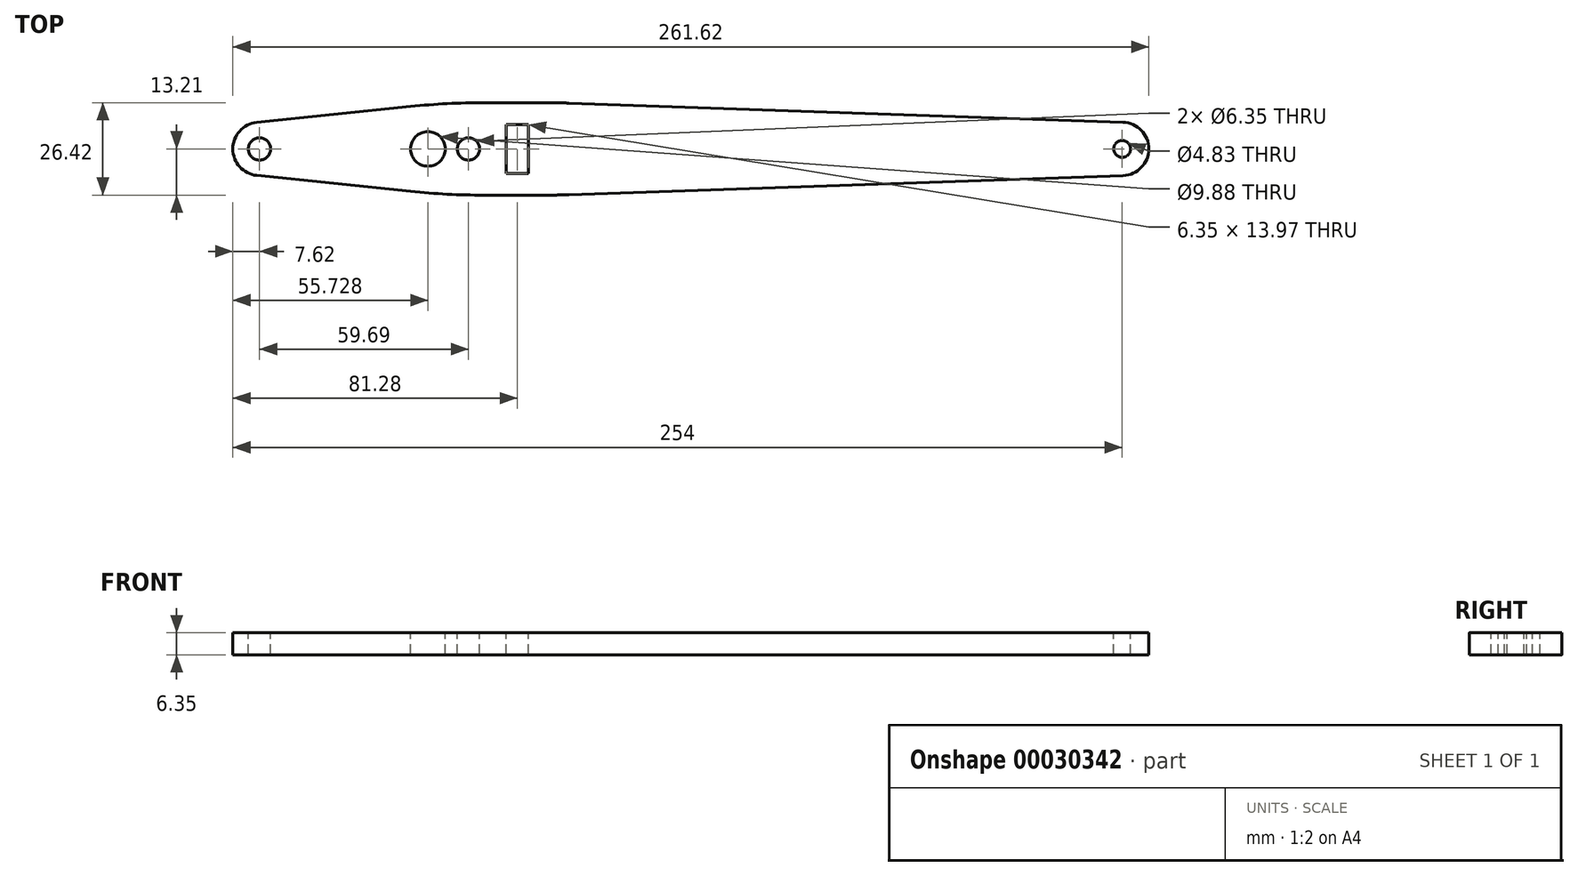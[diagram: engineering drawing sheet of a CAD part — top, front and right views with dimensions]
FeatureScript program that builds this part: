
annotation { "Feature Type Name" : "Feature", "Feature Type Description" : "" }
export const myFeature = defineFeature(function(context is Context, id is Id, definition is map)
    precondition{}
    {
        {
            var Q0;
            Q0=qCreatedBy(makeId("Top.planeOp"),FACE);
            var sketch = newSketch(context, id + "F0", { "sketchPlane" : qUnion([Q0])});
            skFitSpline(sketch, "E0", {"points": [v(101.6, 0.22) * mm, v(96.52, 1.43) * mm, v(91.44, 2.57) * mm, v(81.28, 4.66) * mm, v(71.12, 6.51) * mm, v(60.96, 8.11) * mm, v(50.8, 9.41) * mm, v(40.64, 10.32) * mm, v(30.48, 10.67) * mm, v(25.4, 10.56) * mm, v(20.32, 10.2) * mm, v(15.24, 9.5) * mm, v(10.16, 8.33) * mm, v(7.62, 7.47) * mm, v(5.08, 6.32) * mm, v(2.54, 4.65) * mm, v(1.27, 3.37) * mm, v(0, 0) * mm, v(1.27, -3.37) * mm, v(2.54, -4.65) * mm, v(5.08, -6.32) * mm, v(7.62, -7.47) * mm, v(10.16, -8.33) * mm, v(15.24, -9.5) * mm, v(20.32, -10.2) * mm, v(25.4, -10.56) * mm, v(30.48, -10.67) * mm, v(40.64, -10.32) * mm, v(50.8, -9.41) * mm, v(60.96, -8.11) * mm, v(71.12, -6.51) * mm, v(81.28, -4.66) * mm, v(91.44, -2.57) * mm, v(96.52, -1.43) * mm, v(101.6, -0.22) * mm], "startDerivative": vector(-548.74, 130.7) * mm, "endDerivative": vector(548.74, 130.7) * mm});
            skLineSegment(sketch, "E1", {"start": v(101.6, 0.22) * mm, "end": v(101.6, -0.22) * mm});
            skCircle(sketch, "E2", {"center": v(4.93, 0) * mm, "radius": 4.94 * mm, "construction": true});
            skSolve(sketch);
        }
        {
            var Q0;
            Q0=qCreatedBy(makeId("Top.planeOp"),FACE);
            var sketch = newSketch(context, id + "F1", { "sketchPlane" : qUnion([Q0])});
            skLineSegment(sketch, "E3", {"start": v(20.93, 13.21) * mm, "end": v(38.1, 13.21) * mm});
            skLineSegment(sketch, "E4", {"start": v(45.12, 13.1) * mm, "end": v(203.46, 7.62) * mm});
            skLineSegment(sketch, "E5", {"start": v(0, 12.13) * mm, "end": v(-43.96, 7.58) * mm});
            skArc(sketch, "E6", {"start": v(-43.96, 7.58) * mm, "mid": v(-48.84, 5.1) * mm, "end": v(-50.8, 0) * mm});
            skArc(sketch, "E7", {"start": v(203.46, 7.62) * mm, "mid": v(208.68, 5.3) * mm, "end": v(210.82, 0) * mm});
            skPoint(sketch, "E8.visualSharp", {"position": v(10.44, 13.21) * mm});
            skArc(sketch, "E8.filletArc", {"start": v(20.93, 13.21) * mm, "mid": v(10.45, 12.94) * mm, "end": v(0, 12.13) * mm});
            skPoint(sketch, "E9.visualSharp", {"position": v(41.61, 13.21) * mm});
            skArc(sketch, "E9.filletArc", {"start": v(45.12, 13.1) * mm, "mid": v(41.61, 13.18) * mm, "end": v(38.1, 13.21) * mm});
            skArc(sketch, "E10.MirrorCS", {"start": v(203.46, -7.62) * mm, "mid": v(208.68, -5.3) * mm, "end": v(210.82, 0) * mm});
            skLineSegment(sketch, "E11.MirrorCS", {"start": v(45.12, -13.1) * mm, "end": v(203.46, -7.62) * mm});
            skArc(sketch, "E12.MirrorCS", {"start": v(45.12, -13.1) * mm, "mid": v(41.61, -13.18) * mm, "end": v(38.1, -13.21) * mm});
            skLineSegment(sketch, "E13.MirrorCS", {"start": v(0, -12.13) * mm, "end": v(-43.96, -7.58) * mm});
            skLineSegment(sketch, "E14.MirrorCS", {"start": v(20.93, -13.21) * mm, "end": v(38.1, -13.21) * mm});
            skArc(sketch, "E15.MirrorCS", {"start": v(20.93, -13.21) * mm, "mid": v(10.45, -12.94) * mm, "end": v(0, -12.13) * mm});
            skArc(sketch, "E16.MirrorCS", {"start": v(-43.96, -7.58) * mm, "mid": v(-48.84, -5.1) * mm, "end": v(-50.8, 0) * mm});
            skSolve(sketch);
        }
        {
            var Q0;
            Q0 = qSketchRegion(id + "F1", true);
            extrude(context, id + "F2", {"entities" : qUnion([Q0]), "oppositeDirection" : true, "depth" : 6.35 * mm});
        }
        {
            var Q0;
            Q0=makeQuery(id+"F2.opExtrude","CAP_FACE",FACE,{"disambiguationData":[OSD([sQuery(id+"F1.wireOp",EDGE,"E3"),sQuery(id+"F1.wireOp",EDGE,"E4"),sQuery(id+"F1.wireOp",EDGE,"E5"),sQuery(id+"F1.wireOp",EDGE,"E6"),sQuery(id+"F1.wireOp",EDGE,"E7"),sQuery(id+"F1.wireOp",EDGE,"E8.filletArc"),sQuery(id+"F1.wireOp",EDGE,"E9.filletArc"),sQuery(id+"F1.wireOp",EDGE,"E10.MirrorCS"),sQuery(id+"F1.wireOp",EDGE,"E11.MirrorCS"),sQuery(id+"F1.wireOp",EDGE,"E12.MirrorCS"),sQuery(id+"F1.wireOp",EDGE,"E13.MirrorCS"),sQuery(id+"F1.wireOp",EDGE,"E14.MirrorCS"),sQuery(id+"F1.wireOp",EDGE,"E15.MirrorCS"),sQuery(id+"F1.wireOp",EDGE,"E16.MirrorCS")])],"isStart":true});
            var sketch = newSketch(context, id + "F3", { "sketchPlane" : qUnion([Q0])});
            skCircle(sketch, "E17", {"center": v(-43.18, 0) * mm, "radius": 3.18 * mm});
            skCircle(sketch, "E18", {"center": v(16.51, 0) * mm, "radius": 3.18 * mm});
            skCircle(sketch, "E19", {"center": v(4.93, 0) * mm, "radius": 4.94 * mm});
            skCircle(sketch, "E20", {"center": v(203.2, 0) * mm, "radius": 2.41 * mm});
            skSolve(sketch);
        }
        {
            var Q0;
            Q0 = qSketchRegion(id + "F3", true);
            extrude(context, id + "F4", {"entities" : qUnion([Q0]), "operationType" : NewBodyOperationType.REMOVE, "endBound" : BoundingType.UP_TO_NEXT, "oppositeDirection" : true, "depth" : 25.4 * mm});
        }
        {
            var Q0;
            Q0=makeQuery(id+"F2.opExtrude","CAP_FACE",FACE,{"disambiguationData":[OSD([sQuery(id+"F1.wireOp",EDGE,"E3"),sQuery(id+"F1.wireOp",EDGE,"E4"),sQuery(id+"F1.wireOp",EDGE,"E5"),sQuery(id+"F1.wireOp",EDGE,"E6"),sQuery(id+"F1.wireOp",EDGE,"E7"),sQuery(id+"F1.wireOp",EDGE,"E8.filletArc"),sQuery(id+"F1.wireOp",EDGE,"E9.filletArc"),sQuery(id+"F1.wireOp",EDGE,"E10.MirrorCS"),sQuery(id+"F1.wireOp",EDGE,"E11.MirrorCS"),sQuery(id+"F1.wireOp",EDGE,"E12.MirrorCS"),sQuery(id+"F1.wireOp",EDGE,"E13.MirrorCS"),sQuery(id+"F1.wireOp",EDGE,"E14.MirrorCS"),sQuery(id+"F1.wireOp",EDGE,"E15.MirrorCS"),sQuery(id+"F1.wireOp",EDGE,"E16.MirrorCS")])],"isStart":true});
            var sketch = newSketch(context, id + "F5", { "sketchPlane" : qUnion([Q0])});
            skLineSegment(sketch, "E21.bottom", {"start": v(27.3, 6.99) * mm, "end": v(33.65, 6.99) * mm});
            skLineSegment(sketch, "E21.top", {"start": v(27.3, -6.99) * mm, "end": v(33.65, -6.99) * mm});
            skLineSegment(sketch, "E21.left", {"start": v(27.3, 6.99) * mm, "end": v(27.3, -6.99) * mm});
            skLineSegment(sketch, "E21.right", {"start": v(33.65, 6.99) * mm, "end": v(33.65, -6.99) * mm});
            skPoint(sketch, "E22", {"position": v(30.48, 6.99) * mm});
            skSolve(sketch);
        }
        {
            var Q0;
            Q0 = qSketchRegion(id + "F5", true);
            extrude(context, id + "F6", {"entities" : qUnion([Q0]), "operationType" : NewBodyOperationType.REMOVE, "endBound" : BoundingType.UP_TO_NEXT, "oppositeDirection" : true, "depth" : 25.4 * mm});
        }
    });
